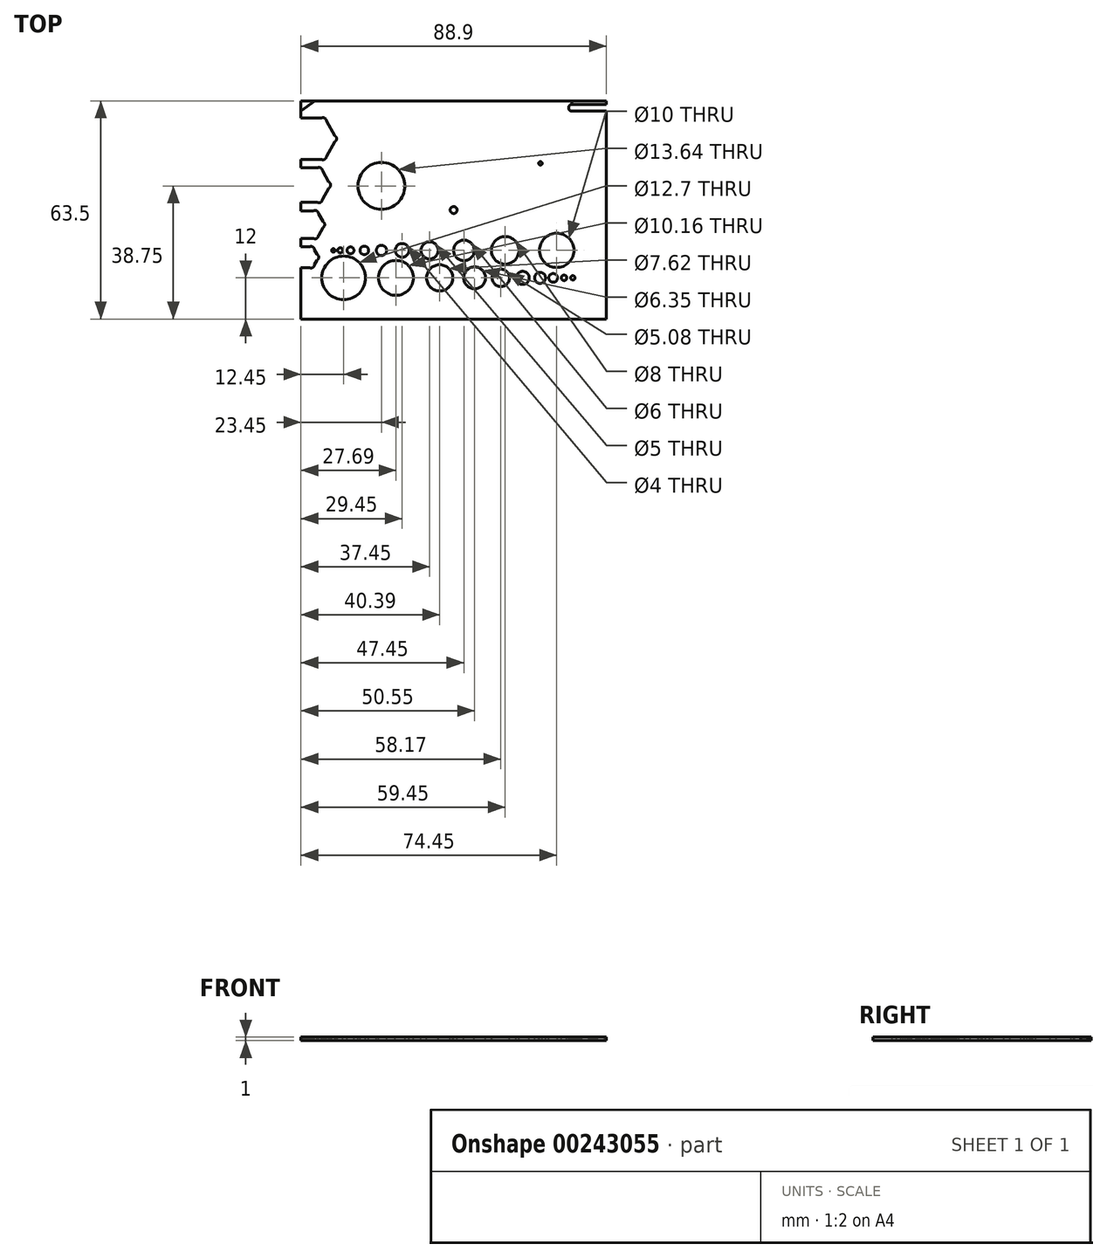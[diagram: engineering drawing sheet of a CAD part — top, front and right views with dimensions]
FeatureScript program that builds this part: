
annotation { "Feature Type Name" : "Feature", "Feature Type Description" : "" }
export const myFeature = defineFeature(function(context is Context, id is Id, definition is map)
    precondition{}
    {
        {
            var Q0;
            Q0=qCreatedBy(makeId("Top.planeOp"),FACE);
            var sketch = newSketch(context, id + "F0", { "sketchPlane" : qUnion([Q0])});
            skLineSegment(sketch, "E0.bottom", {"start": v(0, 0) * mm, "end": v(88.9, 0) * mm});
            skLineSegment(sketch, "E0.top", {"start": v(0, 63.5) * mm, "end": v(88.9, 63.5) * mm});
            skLineSegment(sketch, "E0.left", {"start": v(0, 0) * mm, "end": v(0, 63.5) * mm});
            skLineSegment(sketch, "E0.right", {"start": v(88.9, 0) * mm, "end": v(88.9, 63.5) * mm});
            skSolve(sketch);
        }
        {
            var Q0;
            Q0 = qSketchRegion(id + "F0", true);
            extrude(context, id + "F1", {"entities" : qUnion([Q0]), "depth" : 1 * mm});
        }
        {
            var Q0;
            Q0=makeQuery(id+"F1.opExtrude","CAP_FACE",FACE,{"disambiguationData":[OSD([sQuery(id+"F0.wireOp",EDGE,"E0.bottom"),sQuery(id+"F0.wireOp",EDGE,"E0.top"),sQuery(id+"F0.wireOp",EDGE,"E0.left"),sQuery(id+"F0.wireOp",EDGE,"E0.right")])],"isStart":false});
            var sketch = newSketch(context, id + "F2", { "sketchPlane" : qUnion([Q0])});
            skLineSegment(sketch, "E1", {"start": v(5.4, 0) * mm, "end": v(5.4, 2) * mm});
            skLineSegment(sketch, "E2", {"start": v(6.4, 0) * mm, "end": v(6.4, 1) * mm});
            skLineSegment(sketch, "E3", {"start": v(7.4, 0) * mm, "end": v(7.4, 1) * mm});
            skLineSegment(sketch, "E4", {"start": v(8.4, 0) * mm, "end": v(8.4, 1) * mm});
            skLineSegment(sketch, "E5", {"start": v(9.4, 0) * mm, "end": v(9.4, 1) * mm});
            skLineSegment(sketch, "E6", {"start": v(10.4, 0) * mm, "end": v(10.4, 1.5) * mm});
            skLineSegment(sketch, "E7", {"start": v(11.4, 0) * mm, "end": v(11.4, 1) * mm});
            skLineSegment(sketch, "E8", {"start": v(12.4, 0) * mm, "end": v(12.4, 1) * mm});
            skLineSegment(sketch, "E9", {"start": v(13.4, 0) * mm, "end": v(13.4, 1) * mm});
            skLineSegment(sketch, "E10", {"start": v(14.4, 0) * mm, "end": v(14.4, 1) * mm});
            skLineSegment(sketch, "E11", {"start": v(15.4, 0) * mm, "end": v(15.4, 2) * mm});
            skLineSegment(sketch, "E12.1.0.0", {"start": v(25.4, 0) * mm, "end": v(25.4, 2) * mm});
            skLineSegment(sketch, "E12.1.0.1", {"start": v(20.4, 0) * mm, "end": v(20.4, 1.5) * mm});
            skLineSegment(sketch, "E12.1.0.2", {"start": v(25.4, 0) * mm, "end": v(25.4, 2) * mm});
            skLineSegment(sketch, "E12.1.0.3", {"start": v(24.4, 0) * mm, "end": v(24.4, 1) * mm});
            skLineSegment(sketch, "E12.1.0.4", {"start": v(23.4, 0) * mm, "end": v(23.4, 1) * mm});
            skLineSegment(sketch, "E12.1.0.5", {"start": v(22.4, 0) * mm, "end": v(22.4, 1) * mm});
            skLineSegment(sketch, "E12.1.0.6", {"start": v(21.4, 0) * mm, "end": v(21.4, 1) * mm});
            skLineSegment(sketch, "E12.1.0.7", {"start": v(19.4, 0) * mm, "end": v(19.4, 1) * mm});
            skLineSegment(sketch, "E12.1.0.8", {"start": v(18.4, 0) * mm, "end": v(18.4, 1) * mm});
            skLineSegment(sketch, "E12.1.0.9", {"start": v(17.4, 0) * mm, "end": v(17.4, 1) * mm});
            skLineSegment(sketch, "E12.1.0.10", {"start": v(16.4, 0) * mm, "end": v(16.4, 1) * mm});
            skLineSegment(sketch, "E12.2.0.0", {"start": v(35.4, 0) * mm, "end": v(35.4, 2) * mm});
            skLineSegment(sketch, "E12.2.0.1", {"start": v(30.4, 0) * mm, "end": v(30.4, 1.5) * mm});
            skLineSegment(sketch, "E12.2.0.2", {"start": v(35.4, 0) * mm, "end": v(35.4, 2) * mm});
            skLineSegment(sketch, "E12.2.0.3", {"start": v(34.4, 0) * mm, "end": v(34.4, 1) * mm});
            skLineSegment(sketch, "E12.2.0.4", {"start": v(33.4, 0) * mm, "end": v(33.4, 1) * mm});
            skLineSegment(sketch, "E12.2.0.5", {"start": v(32.4, 0) * mm, "end": v(32.4, 1) * mm});
            skLineSegment(sketch, "E12.2.0.6", {"start": v(31.4, 0) * mm, "end": v(31.4, 1) * mm});
            skLineSegment(sketch, "E12.2.0.7", {"start": v(29.4, 0) * mm, "end": v(29.4, 1) * mm});
            skLineSegment(sketch, "E12.2.0.8", {"start": v(28.4, 0) * mm, "end": v(28.4, 1) * mm});
            skLineSegment(sketch, "E12.2.0.9", {"start": v(27.4, 0) * mm, "end": v(27.4, 1) * mm});
            skLineSegment(sketch, "E12.2.0.10", {"start": v(26.4, 0) * mm, "end": v(26.4, 1) * mm});
            skLineSegment(sketch, "E12.3.0.0", {"start": v(45.4, 0) * mm, "end": v(45.4, 2) * mm});
            skLineSegment(sketch, "E12.3.0.1", {"start": v(40.4, 0) * mm, "end": v(40.4, 1.5) * mm});
            skLineSegment(sketch, "E12.3.0.2", {"start": v(45.4, 0) * mm, "end": v(45.4, 2) * mm});
            skLineSegment(sketch, "E12.3.0.3", {"start": v(44.4, 0) * mm, "end": v(44.4, 1) * mm});
            skLineSegment(sketch, "E12.3.0.4", {"start": v(43.4, 0) * mm, "end": v(43.4, 1) * mm});
            skLineSegment(sketch, "E12.3.0.5", {"start": v(42.4, 0) * mm, "end": v(42.4, 1) * mm});
            skLineSegment(sketch, "E12.3.0.6", {"start": v(41.4, 0) * mm, "end": v(41.4, 1) * mm});
            skLineSegment(sketch, "E12.3.0.7", {"start": v(39.4, 0) * mm, "end": v(39.4, 1) * mm});
            skLineSegment(sketch, "E12.3.0.8", {"start": v(38.4, 0) * mm, "end": v(38.4, 1) * mm});
            skLineSegment(sketch, "E12.3.0.9", {"start": v(37.4, 0) * mm, "end": v(37.4, 1) * mm});
            skLineSegment(sketch, "E12.3.0.10", {"start": v(36.4, 0) * mm, "end": v(36.4, 1) * mm});
            skLineSegment(sketch, "E12.4.0.0", {"start": v(55.4, 0) * mm, "end": v(55.4, 2) * mm});
            skLineSegment(sketch, "E12.4.0.1", {"start": v(50.4, 0) * mm, "end": v(50.4, 1.5) * mm});
            skLineSegment(sketch, "E12.4.0.2", {"start": v(55.4, 0) * mm, "end": v(55.4, 2) * mm});
            skLineSegment(sketch, "E12.4.0.3", {"start": v(54.4, 0) * mm, "end": v(54.4, 1) * mm});
            skLineSegment(sketch, "E12.4.0.4", {"start": v(53.4, 0) * mm, "end": v(53.4, 1) * mm});
            skLineSegment(sketch, "E12.4.0.5", {"start": v(52.4, 0) * mm, "end": v(52.4, 1) * mm});
            skLineSegment(sketch, "E12.4.0.6", {"start": v(51.4, 0) * mm, "end": v(51.4, 1) * mm});
            skLineSegment(sketch, "E12.4.0.7", {"start": v(49.4, 0) * mm, "end": v(49.4, 1) * mm});
            skLineSegment(sketch, "E12.4.0.8", {"start": v(48.4, 0) * mm, "end": v(48.4, 1) * mm});
            skLineSegment(sketch, "E12.4.0.9", {"start": v(47.4, 0) * mm, "end": v(47.4, 1) * mm});
            skLineSegment(sketch, "E12.4.0.10", {"start": v(46.4, 0) * mm, "end": v(46.4, 1) * mm});
            skLineSegment(sketch, "E12.5.0.0", {"start": v(65.4, 0) * mm, "end": v(65.4, 2) * mm});
            skLineSegment(sketch, "E12.5.0.1", {"start": v(60.4, 0) * mm, "end": v(60.4, 1.5) * mm});
            skLineSegment(sketch, "E12.5.0.2", {"start": v(65.4, 0) * mm, "end": v(65.4, 2) * mm});
            skLineSegment(sketch, "E12.5.0.3", {"start": v(64.4, 0) * mm, "end": v(64.4, 1) * mm});
            skLineSegment(sketch, "E12.5.0.4", {"start": v(63.4, 0) * mm, "end": v(63.4, 1) * mm});
            skLineSegment(sketch, "E12.5.0.5", {"start": v(62.4, 0) * mm, "end": v(62.4, 1) * mm});
            skLineSegment(sketch, "E12.5.0.6", {"start": v(61.4, 0) * mm, "end": v(61.4, 1) * mm});
            skLineSegment(sketch, "E12.5.0.7", {"start": v(59.4, 0) * mm, "end": v(59.4, 1) * mm});
            skLineSegment(sketch, "E12.5.0.8", {"start": v(58.4, 0) * mm, "end": v(58.4, 1) * mm});
            skLineSegment(sketch, "E12.5.0.9", {"start": v(57.4, 0) * mm, "end": v(57.4, 1) * mm});
            skLineSegment(sketch, "E12.5.0.10", {"start": v(56.4, 0) * mm, "end": v(56.4, 1) * mm});
            skLineSegment(sketch, "E12.6.0.0", {"start": v(75.4, 0) * mm, "end": v(75.4, 2) * mm});
            skLineSegment(sketch, "E12.6.0.1", {"start": v(70.4, 0) * mm, "end": v(70.4, 1.5) * mm});
            skLineSegment(sketch, "E12.6.0.2", {"start": v(75.4, 0) * mm, "end": v(75.4, 2) * mm});
            skLineSegment(sketch, "E12.6.0.3", {"start": v(74.4, 0) * mm, "end": v(74.4, 1) * mm});
            skLineSegment(sketch, "E12.6.0.4", {"start": v(73.4, 0) * mm, "end": v(73.4, 1) * mm});
            skLineSegment(sketch, "E12.6.0.5", {"start": v(72.4, 0) * mm, "end": v(72.4, 1) * mm});
            skLineSegment(sketch, "E12.6.0.6", {"start": v(71.4, 0) * mm, "end": v(71.4, 1) * mm});
            skLineSegment(sketch, "E12.6.0.7", {"start": v(69.4, 0) * mm, "end": v(69.4, 1) * mm});
            skLineSegment(sketch, "E12.6.0.8", {"start": v(68.4, 0) * mm, "end": v(68.4, 1) * mm});
            skLineSegment(sketch, "E12.6.0.9", {"start": v(67.4, 0) * mm, "end": v(67.4, 1) * mm});
            skLineSegment(sketch, "E12.6.0.10", {"start": v(66.4, 0) * mm, "end": v(66.4, 1) * mm});
            skLineSegment(sketch, "E12.7.0.0", {"start": v(85.4, 0) * mm, "end": v(85.4, 2) * mm});
            skLineSegment(sketch, "E12.7.0.1", {"start": v(80.4, 0) * mm, "end": v(80.4, 1.5) * mm});
            skLineSegment(sketch, "E12.7.0.2", {"start": v(85.4, 0) * mm, "end": v(85.4, 2) * mm});
            skLineSegment(sketch, "E12.7.0.3", {"start": v(84.4, 0) * mm, "end": v(84.4, 1) * mm});
            skLineSegment(sketch, "E12.7.0.4", {"start": v(83.4, 0) * mm, "end": v(83.4, 1) * mm});
            skLineSegment(sketch, "E12.7.0.5", {"start": v(82.4, 0) * mm, "end": v(82.4, 1) * mm});
            skLineSegment(sketch, "E12.7.0.6", {"start": v(81.4, 0) * mm, "end": v(81.4, 1) * mm});
            skLineSegment(sketch, "E12.7.0.7", {"start": v(79.4, 0) * mm, "end": v(79.4, 1) * mm});
            skLineSegment(sketch, "E12.7.0.8", {"start": v(78.4, 0) * mm, "end": v(78.4, 1) * mm});
            skLineSegment(sketch, "E12.7.0.9", {"start": v(77.4, 0) * mm, "end": v(77.4, 1) * mm});
            skLineSegment(sketch, "E12.7.0.10", {"start": v(76.4, 0) * mm, "end": v(76.4, 1) * mm});
            skLineSegment(sketch, "E12.direction1", {"start": v(6.4, 0) * mm, "end": v(16.4, 0) * mm, "construction": true});
            skLineSegment(sketch, "E13", {"start": v(0, 2.5) * mm, "end": v(88.9, 2.5) * mm, "construction": true});
            skText(sketch, "E14", { "text": "1", "fontName": "NotoSansCJKjp-Regular.otf"});
            skText(sketch, "E15", { "text": "0", "fontName": "NotoSansCJKjp-Regular.otf"});
            skText(sketch, "E16", { "text": "2", "fontName": "NotoSansCJKjp-Regular.otf"});
            skText(sketch, "E17", { "text": "3", "fontName": "NotoSansCJKjp-Regular.otf"});
            skText(sketch, "E18", { "text": "4", "fontName": "NotoSansCJKjp-Regular.otf"});
            skText(sketch, "E19", { "text": "5", "fontName": "NotoSansCJKjp-Regular.otf"});
            skText(sketch, "E20", { "text": "6", "fontName": "NotoSansCJKjp-Regular.otf"});
            skText(sketch, "E21", { "text": "7", "fontName": "NotoSansCJKjp-Regular.otf"});
            skText(sketch, "E22", { "text": "8", "fontName": "NotoSansCJKjp-Regular.otf"});
            const initialGuessF2  = {"E14": [0.0148, 0.0025, 1, 0, 0.0016], "E15": [0.00478, 0.0025, 1, 0, 0.00158], "E16": [0.02479, 0.0025, 1, 0, 0.00158], "E17": [0.03479, 0.0025, 1, 0, 0.00158], "E18": [0.04477, 0.0025, 1, 0, 0.00156], "E19": [0.05479, 0.0025, 1, 0, 0.00158], "E20": [0.06478, 0.0025, 1, 0, 0.00157], "E21": [0.07478, 0.0025, 1, 0, 0.00157], "E22": [0.08478, 0.0025, 1, 0, 0.00157]};
            skSetInitialGuess(sketch, initialGuessF2);
            skSolve(sketch);
        }
        {
            var Q0;
            Q0=makeQuery(id+"F1.opExtrude","CAP_FACE",FACE,{"disambiguationData":[OSD([sQuery(id+"F0.wireOp",EDGE,"E0.bottom"),sQuery(id+"F0.wireOp",EDGE,"E0.top"),sQuery(id+"F0.wireOp",EDGE,"E0.left"),sQuery(id+"F0.wireOp",EDGE,"E0.right")])],"isStart":true});
            var sketch = newSketch(context, id + "F3", { "sketchPlane" : qUnion([Q0])});
            skPoint(sketch, "E23.0", {"position": v(5.4, -2) * mm});
            skPoint(sketch, "E24.0", {"position": v(10.4, -1.5) * mm});
            skLineSegment(sketch, "E25.0", {"start": v(0, -2.5) * mm, "end": v(88.9, -2.5) * mm});
            skPoint(sketch, "E26.0", {"position": v(6.4, -1) * mm});
            skLineSegment(sketch, "E27", {"start": v(5.4, -2) * mm, "end": v(5.4, 0) * mm});
            skLineSegment(sketch, "E28", {"start": v(10.48, 0) * mm, "end": v(10.48, -1) * mm});
            skLineSegment(sketch, "E29", {"start": v(7.94, 0) * mm, "end": v(7.94, -1) * mm});
            skLineSegment(sketch, "E30", {"start": v(13.02, 0) * mm, "end": v(13.02, -1) * mm});
            skLineSegment(sketch, "E31", {"start": v(15.56, 0) * mm, "end": v(15.56, -1) * mm});
            skLineSegment(sketch, "E32", {"start": v(18.1, 0) * mm, "end": v(18.1, -1.5) * mm});
            skLineSegment(sketch, "E33", {"start": v(20.64, 0) * mm, "end": v(20.64, -1) * mm});
            skLineSegment(sketch, "E34", {"start": v(23.18, 0) * mm, "end": v(23.18, -1) * mm});
            skLineSegment(sketch, "E35", {"start": v(25.72, 0) * mm, "end": v(25.72, -1) * mm});
            skLineSegment(sketch, "E36", {"start": v(28.26, 0) * mm, "end": v(28.26, -1) * mm});
            skLineSegment(sketch, "E37", {"start": v(30.8, 0) * mm, "end": v(30.8, -2) * mm});
            skPoint(sketch, "E38.1.0.0", {"position": v(31.8, -1) * mm});
            skPoint(sketch, "E38.1.0.1", {"position": v(35.8, -1.5) * mm});
            skLineSegment(sketch, "E38.1.0.2", {"start": v(56.2, 0) * mm, "end": v(56.2, -2) * mm});
            skLineSegment(sketch, "E38.1.0.3", {"start": v(38.42, 0) * mm, "end": v(38.42, -1) * mm});
            skLineSegment(sketch, "E38.1.0.4", {"start": v(51.12, 0) * mm, "end": v(51.12, -1) * mm});
            skLineSegment(sketch, "E38.1.0.5", {"start": v(40.96, 0) * mm, "end": v(40.96, -1) * mm});
            skLineSegment(sketch, "E38.1.0.6", {"start": v(43.5, 0) * mm, "end": v(43.5, -1.5) * mm});
            skLineSegment(sketch, "E38.1.0.7", {"start": v(46.04, 0) * mm, "end": v(46.04, -1) * mm});
            skLineSegment(sketch, "E38.1.0.8", {"start": v(33.34, 0) * mm, "end": v(33.34, -1) * mm});
            skLineSegment(sketch, "E38.1.0.9", {"start": v(35.88, 0) * mm, "end": v(35.88, -1) * mm});
            skLineSegment(sketch, "E38.1.0.10", {"start": v(48.58, 0) * mm, "end": v(48.58, -1) * mm});
            skLineSegment(sketch, "E38.1.0.11", {"start": v(53.66, 0) * mm, "end": v(53.66, -1) * mm});
            skPoint(sketch, "E38.2.0.0", {"position": v(57.2, -1) * mm});
            skPoint(sketch, "E38.2.0.1", {"position": v(61.2, -1.5) * mm});
            skLineSegment(sketch, "E38.2.0.2", {"start": v(81.6, 0) * mm, "end": v(81.6, -2) * mm});
            skLineSegment(sketch, "E38.2.0.3", {"start": v(63.82, 0) * mm, "end": v(63.82, -1) * mm});
            skLineSegment(sketch, "E38.2.0.4", {"start": v(76.52, 0) * mm, "end": v(76.52, -1) * mm});
            skLineSegment(sketch, "E38.2.0.5", {"start": v(66.36, 0) * mm, "end": v(66.36, -1) * mm});
            skLineSegment(sketch, "E38.2.0.6", {"start": v(68.9, 0) * mm, "end": v(68.9, -1.5) * mm});
            skLineSegment(sketch, "E38.2.0.7", {"start": v(71.44, 0) * mm, "end": v(71.44, -1) * mm});
            skLineSegment(sketch, "E38.2.0.8", {"start": v(58.74, 0) * mm, "end": v(58.74, -1) * mm});
            skLineSegment(sketch, "E38.2.0.9", {"start": v(61.28, 0) * mm, "end": v(61.28, -1) * mm});
            skLineSegment(sketch, "E38.2.0.10", {"start": v(73.98, 0) * mm, "end": v(73.98, -1) * mm});
            skLineSegment(sketch, "E38.2.0.11", {"start": v(79.06, 0) * mm, "end": v(79.06, -1) * mm});
            skLineSegment(sketch, "E38.direction1", {"start": v(6.4, -1) * mm, "end": v(31.8, -1) * mm, "construction": true});
            skText(sketch, "E39", { "text": "0", "fontName": "NotoSansCJKjp-Regular.otf"});
            skText(sketch, "E40", { "text": "1", "fontName": "NotoSansCJKjp-Regular.otf"});
            skText(sketch, "E41", { "text": "2", "fontName": "NotoSansCJKjp-Regular.otf"});
            skText(sketch, "E42", { "text": "3", "fontName": "NotoSansCJKjp-Regular.otf"});
            const initialGuessF3  = {"E39": [0.00478, -0.00408, 1, 0, 0.00158], "E40": [0.0302, -0.0041, 1, 0, 0.0016], "E41": [0.05559, -0.00408, 1, 0, 0.00158], "E42": [0.08099, -0.00408, 1, 0, 0.00158]};
            skSetInitialGuess(sketch, initialGuessF3);
            skSolve(sketch);
        }
        {
            var Q0;
            Q0=makeQuery(id+"F2.imprint","IMPRINT",FACE,{"disambiguationData":[TD([[makeQuery(id+"F2.imprint","IMPRINT",EDGE,{"derivedFrom":sQuery(id+"F2.wireOp",EDGE,"E14.sketch_text.stroke-0")}),-1.0]])]});
            var sketch = newSketch(context, id + "F4", { "sketchPlane" : qUnion([Q0])});
            skLineSegment(sketch, "E43.0", {"start": v(88.9, 0) * mm, "end": v(88.9, 63.5) * mm});
            skLineSegment(sketch, "E44.0", {"start": v(0, 0) * mm, "end": v(88.9, 0) * mm});
            skLineSegment(sketch, "E45", {"start": v(88.9, 31.75) * mm, "end": v(0, 31.75) * mm, "construction": true});
            skLineSegment(sketch, "E46", {"start": v(88.9, 62.5) * mm, "end": v(78.9, 62.5) * mm});
            skLineSegment(sketch, "E47", {"start": v(78.9, 62.5) * mm, "end": v(78.9, 60.5) * mm});
            skLineSegment(sketch, "E48", {"start": v(78.9, 60.5) * mm, "end": v(88.9, 60.5) * mm});
            skCircle(sketch, "E49", {"center": v(78.9, 61.5) * mm, "radius": 1 * mm});
            skSolve(sketch);
        }
        {
            var Q0;
            Q0 = qSketchRegion(id + "F4", true);
            extrude(context, id + "F5", {"entities" : qUnion([Q0]), "operationType" : NewBodyOperationType.REMOVE, "oppositeDirection" : true, "depth" : 25 * mm});
        }
        {
            var Q0;
            {var subQ0=sQuery(id+"F0.wireOp",EDGE,"E0.bottom");var subQ1=sQuery(id+"F0.wireOp",EDGE,"E0.right");Q0=makeQuery(id+"F5.boolean.opBoolean","SPLIT",FACE,{"disambiguationData":[TD([makeQuery(id+"F1.opExtrude","SWEPT_FACE",FACE,{"disambiguationData":[OSD([subQ0])]})])],"derivedFrom":makeQuery(id+"F1.opExtrude","SWEPT_FACE",FACE,{"disambiguationData":[OSD([subQ1])]})});}
            var sketch = newSketch(context, id + "F6", { "sketchPlane" : qUnion([Q0])});
            skLineSegment(sketch, "E50.0.0", {"start": v(62.5, 1) * mm, "end": v(62.5, 0) * mm});
            skLineSegment(sketch, "E50.0.1", {"start": v(62.5, 0) * mm, "end": v(63.5, 0) * mm});
            skLineSegment(sketch, "E50.0.2", {"start": v(63.5, 0) * mm, "end": v(63.5, 1) * mm});
            skLineSegment(sketch, "E50.0.3", {"start": v(63.5, 1) * mm, "end": v(62.5, 1) * mm});
            skPoint(sketch, "E51.endSnap0", {"position": v(63.5, 0.5) * mm});
            skPoint(sketch, "E52.endSnap0", {"position": v(63, 1) * mm});
            skLineSegment(sketch, "E53.0.0", {"start": v(62.5, 0) * mm, "end": v(62.5, 1) * mm});
            skPoint(sketch, "E54", {"position": v(62.5, 0.5) * mm});
            skEllipse(sketch, "E55", {"center": v(62.5, 1) * mm, "majorRadius": 1 * mm, "minorRadius": 0.5 * mm, "majorAxis": v(1, 0)});
            skEllipse(sketch, "E56", {"center": v(62.5, 0) * mm, "majorRadius": 1 * mm, "minorRadius": 0.5 * mm, "majorAxis": v(1, 0)});
            skSolve(sketch);
        }
        {
            var Q0;
            {var subQ0=sQuery(id+"F6.wireOp",EDGE,"E50.0.1");Q0=makeQuery(id+"F6.imprint","IMPRINT",FACE,{"disambiguationData":[TD([[makeQuery(id+"F6.imprint","IMPRINT",EDGE,{"derivedFrom":subQ0}),1.0]])]});}
            var Q1;
            {var subQ0=sQuery(id+"F6.wireOp",EDGE,"E50.0.3");Q1=makeQuery(id+"F6.imprint","IMPRINT",FACE,{"disambiguationData":[TD([[makeQuery(id+"F6.imprint","IMPRINT",EDGE,{"derivedFrom":subQ0}),1.0]])]});}
            extrude(context, id + "F7", {"entities" : qUnion([Q0, Q1]), "operationType" : NewBodyOperationType.REMOVE, "oppositeDirection" : true, "depth" : 10 * mm});
        }
        {
            var Q0;
            Q0=makeQuery(id+"F2.imprint","IMPRINT",FACE,{"disambiguationData":[TD([[makeQuery(id+"F2.imprint","IMPRINT",EDGE,{"derivedFrom":sQuery(id+"F2.wireOp",EDGE,"E14.sketch_text.stroke-0")}),-1.0]])]});
            var sketch = newSketch(context, id + "F8", { "sketchPlane" : qUnion([Q0])});
            skLineSegment(sketch, "E57.0.0", {"start": v(88.9, 63.5) * mm, "end": v(0, 63.5) * mm});
            skLineSegment(sketch, "E57.0.1", {"start": v(-4.62, 60.5) * mm, "end": v(50.37, 28.75) * mm, "construction": true});
            skLineSegment(sketch, "E57.0.2", {"start": v(0, 0) * mm, "end": v(5.4, 0) * mm});
            skLineSegment(sketch, "E57.0.3", {"start": v(5.4, 0) * mm, "end": v(6.4, 0) * mm});
            skLineSegment(sketch, "E57.0.4", {"start": v(6.4, 0) * mm, "end": v(7.4, 0) * mm});
            skLineSegment(sketch, "E57.0.5", {"start": v(7.4, 0) * mm, "end": v(8.4, 0) * mm});
            skLineSegment(sketch, "E57.0.6", {"start": v(8.4, 0) * mm, "end": v(9.4, 0) * mm});
            skLineSegment(sketch, "E57.0.7", {"start": v(9.4, 0) * mm, "end": v(10.4, 0) * mm});
            skLineSegment(sketch, "E57.0.8", {"start": v(10.4, 0) * mm, "end": v(11.4, 0) * mm});
            skLineSegment(sketch, "E57.0.9", {"start": v(11.4, 0) * mm, "end": v(12.4, 0) * mm});
            skLineSegment(sketch, "E57.0.10", {"start": v(12.4, 0) * mm, "end": v(13.4, 0) * mm});
            skLineSegment(sketch, "E57.0.11", {"start": v(13.4, 0) * mm, "end": v(14.4, 0) * mm});
            skLineSegment(sketch, "E57.0.12", {"start": v(14.4, 0) * mm, "end": v(15.4, 0) * mm});
            skLineSegment(sketch, "E57.0.13", {"start": v(15.4, 0) * mm, "end": v(16.4, 0) * mm});
            skLineSegment(sketch, "E57.0.14", {"start": v(16.4, 0) * mm, "end": v(17.4, 0) * mm});
            skLineSegment(sketch, "E57.0.15", {"start": v(17.4, 0) * mm, "end": v(18.4, 0) * mm});
            skLineSegment(sketch, "E57.0.16", {"start": v(18.4, 0) * mm, "end": v(19.4, 0) * mm});
            skLineSegment(sketch, "E57.0.17", {"start": v(19.4, 0) * mm, "end": v(20.4, 0) * mm});
            skLineSegment(sketch, "E57.0.18", {"start": v(20.4, 0) * mm, "end": v(21.4, 0) * mm});
            skLineSegment(sketch, "E57.0.19", {"start": v(21.4, 0) * mm, "end": v(22.4, 0) * mm});
            skLineSegment(sketch, "E57.0.20", {"start": v(22.4, 0) * mm, "end": v(23.4, 0) * mm});
            skLineSegment(sketch, "E57.0.21", {"start": v(23.4, 0) * mm, "end": v(24.4, 0) * mm});
            skLineSegment(sketch, "E57.0.22", {"start": v(24.4, 0) * mm, "end": v(25.4, 0) * mm});
            skLineSegment(sketch, "E57.0.23", {"start": v(25.4, 0) * mm, "end": v(26.4, 0) * mm});
            skLineSegment(sketch, "E57.0.24", {"start": v(26.4, 0) * mm, "end": v(27.4, 0) * mm});
            skLineSegment(sketch, "E57.0.25", {"start": v(27.4, 0) * mm, "end": v(28.4, 0) * mm});
            skLineSegment(sketch, "E57.0.26", {"start": v(28.4, 0) * mm, "end": v(29.4, 0) * mm});
            skLineSegment(sketch, "E57.0.27", {"start": v(29.4, 0) * mm, "end": v(30.4, 0) * mm});
            skLineSegment(sketch, "E57.0.28", {"start": v(30.4, 0) * mm, "end": v(31.4, 0) * mm});
            skLineSegment(sketch, "E57.0.29", {"start": v(31.4, 0) * mm, "end": v(32.4, 0) * mm});
            skLineSegment(sketch, "E57.0.30", {"start": v(32.4, 0) * mm, "end": v(33.4, 0) * mm});
            skLineSegment(sketch, "E57.0.31", {"start": v(33.4, 0) * mm, "end": v(34.4, 0) * mm});
            skLineSegment(sketch, "E57.0.32", {"start": v(34.4, 0) * mm, "end": v(35.4, 0) * mm});
            skLineSegment(sketch, "E57.0.33", {"start": v(35.4, 0) * mm, "end": v(36.4, 0) * mm});
            skLineSegment(sketch, "E57.0.34", {"start": v(36.4, 0) * mm, "end": v(37.4, 0) * mm});
            skLineSegment(sketch, "E57.0.35", {"start": v(37.4, 0) * mm, "end": v(38.4, 0) * mm});
            skLineSegment(sketch, "E57.0.36", {"start": v(38.4, 0) * mm, "end": v(39.4, 0) * mm});
            skLineSegment(sketch, "E57.0.37", {"start": v(39.4, 0) * mm, "end": v(40.4, 0) * mm});
            skLineSegment(sketch, "E57.0.38", {"start": v(40.4, 0) * mm, "end": v(41.4, 0) * mm});
            skLineSegment(sketch, "E57.0.39", {"start": v(41.4, 0) * mm, "end": v(42.4, 0) * mm});
            skLineSegment(sketch, "E57.0.40", {"start": v(42.4, 0) * mm, "end": v(43.4, 0) * mm});
            skLineSegment(sketch, "E57.0.41", {"start": v(43.4, 0) * mm, "end": v(44.4, 0) * mm});
            skLineSegment(sketch, "E57.0.42", {"start": v(44.4, 0) * mm, "end": v(45.4, 0) * mm});
            skLineSegment(sketch, "E57.0.43", {"start": v(45.4, 0) * mm, "end": v(46.4, 0) * mm});
            skLineSegment(sketch, "E57.0.44", {"start": v(46.4, 0) * mm, "end": v(47.4, 0) * mm});
            skLineSegment(sketch, "E57.0.45", {"start": v(47.4, 0) * mm, "end": v(48.4, 0) * mm});
            skLineSegment(sketch, "E57.0.46", {"start": v(48.4, 0) * mm, "end": v(49.4, 0) * mm});
            skLineSegment(sketch, "E57.0.47", {"start": v(49.4, 0) * mm, "end": v(50.4, 0) * mm});
            skLineSegment(sketch, "E57.0.48", {"start": v(50.4, 0) * mm, "end": v(51.4, 0) * mm});
            skLineSegment(sketch, "E57.0.49", {"start": v(51.4, 0) * mm, "end": v(52.4, 0) * mm});
            skLineSegment(sketch, "E57.0.50", {"start": v(52.4, 0) * mm, "end": v(53.4, 0) * mm});
            skLineSegment(sketch, "E57.0.51", {"start": v(53.4, 0) * mm, "end": v(54.4, 0) * mm});
            skLineSegment(sketch, "E57.0.52", {"start": v(54.4, 0) * mm, "end": v(55.4, 0) * mm});
            skLineSegment(sketch, "E57.0.53", {"start": v(55.4, 0) * mm, "end": v(56.4, 0) * mm});
            skLineSegment(sketch, "E57.0.54", {"start": v(56.4, 0) * mm, "end": v(57.4, 0) * mm});
            skLineSegment(sketch, "E57.0.55", {"start": v(57.4, 0) * mm, "end": v(58.4, 0) * mm});
            skLineSegment(sketch, "E57.0.56", {"start": v(58.4, 0) * mm, "end": v(59.4, 0) * mm});
            skLineSegment(sketch, "E57.0.57", {"start": v(59.4, 0) * mm, "end": v(60.4, 0) * mm});
            skLineSegment(sketch, "E57.0.58", {"start": v(60.4, 0) * mm, "end": v(61.4, 0) * mm});
            skLineSegment(sketch, "E57.0.59", {"start": v(61.4, 0) * mm, "end": v(62.4, 0) * mm});
            skLineSegment(sketch, "E57.0.60", {"start": v(62.4, 0) * mm, "end": v(63.4, 0) * mm});
            skLineSegment(sketch, "E57.0.61", {"start": v(63.4, 0) * mm, "end": v(64.4, 0) * mm});
            skLineSegment(sketch, "E57.0.62", {"start": v(64.4, 0) * mm, "end": v(65.4, 0) * mm});
            skLineSegment(sketch, "E57.0.63", {"start": v(65.4, 0) * mm, "end": v(66.4, 0) * mm});
            skLineSegment(sketch, "E57.0.64", {"start": v(66.4, 0) * mm, "end": v(67.4, 0) * mm});
            skLineSegment(sketch, "E57.0.65", {"start": v(67.4, 0) * mm, "end": v(68.4, 0) * mm});
            skLineSegment(sketch, "E57.0.66", {"start": v(68.4, 0) * mm, "end": v(69.4, 0) * mm});
            skLineSegment(sketch, "E57.0.67", {"start": v(69.4, 0) * mm, "end": v(70.4, 0) * mm});
            skLineSegment(sketch, "E57.0.68", {"start": v(70.4, 0) * mm, "end": v(71.4, 0) * mm});
            skLineSegment(sketch, "E57.0.69", {"start": v(71.4, 0) * mm, "end": v(72.4, 0) * mm});
            skLineSegment(sketch, "E57.0.70", {"start": v(72.4, 0) * mm, "end": v(73.4, 0) * mm});
            skLineSegment(sketch, "E57.0.71", {"start": v(73.4, 0) * mm, "end": v(74.4, 0) * mm});
            skLineSegment(sketch, "E57.0.72", {"start": v(74.4, 0) * mm, "end": v(75.4, 0) * mm});
            skLineSegment(sketch, "E57.0.73", {"start": v(75.4, 0) * mm, "end": v(76.4, 0) * mm});
            skLineSegment(sketch, "E57.0.74", {"start": v(76.4, 0) * mm, "end": v(77.4, 0) * mm});
            skLineSegment(sketch, "E57.0.75", {"start": v(77.4, 0) * mm, "end": v(78.4, 0) * mm});
            skLineSegment(sketch, "E57.0.76", {"start": v(78.4, 0) * mm, "end": v(79.4, 0) * mm});
            skLineSegment(sketch, "E57.0.77", {"start": v(79.4, 0) * mm, "end": v(80.4, 0) * mm});
            skLineSegment(sketch, "E57.0.78", {"start": v(80.4, 0) * mm, "end": v(81.4, 0) * mm});
            skLineSegment(sketch, "E57.0.79", {"start": v(81.4, 0) * mm, "end": v(82.4, 0) * mm});
            skLineSegment(sketch, "E57.0.80", {"start": v(82.4, 0) * mm, "end": v(83.4, 0) * mm});
            skLineSegment(sketch, "E57.0.81", {"start": v(83.4, 0) * mm, "end": v(84.4, 0) * mm});
            skLineSegment(sketch, "E57.0.82", {"start": v(84.4, 0) * mm, "end": v(85.4, 0) * mm});
            skLineSegment(sketch, "E57.0.83", {"start": v(85.4, 0) * mm, "end": v(88.9, 0) * mm});
            skLineSegment(sketch, "E57.0.84", {"start": v(88.9, 0) * mm, "end": v(88.9, 63.5) * mm});
            skCircle(sketch, "E58.cCircle", {"center": v(1.73, 18) * mm, "radius": 3 * mm, "construction": true});
            skLineSegment(sketch, "E58.0", {"start": v(2.46, 15) * mm, "end": v(0, 15) * mm});
            skLineSegment(sketch, "E58.1", {"start": v(0, 15) * mm, "end": v(-1.73, 18) * mm});
            skLineSegment(sketch, "E58.2", {"start": v(-1.73, 18) * mm, "end": v(0, 21) * mm});
            skLineSegment(sketch, "E58.3", {"start": v(0, 21) * mm, "end": v(2.46, 21) * mm});
            skLineSegment(sketch, "E58.4", {"start": v(3.96, 20.13) * mm, "end": v(4.7, 18.87) * mm});
            skLineSegment(sketch, "E58.5", {"start": v(4.7, 17.13) * mm, "end": v(3.96, 15.87) * mm});
            skPoint(sketch, "E58.0.midPoint", {"position": v(1.73, 15) * mm});
            skCircle(sketch, "E59.cCircle", {"center": v(2.3, 27.5) * mm, "radius": 4 * mm, "construction": true});
            skLineSegment(sketch, "E59.0", {"start": v(3.62, 23.5) * mm, "end": v(0, 23.5) * mm});
            skLineSegment(sketch, "E59.1", {"start": v(0, 23.5) * mm, "end": v(-2.3, 27.5) * mm});
            skLineSegment(sketch, "E59.2", {"start": v(-2.3, 27.5) * mm, "end": v(0, 31.5) * mm});
            skLineSegment(sketch, "E59.3", {"start": v(0, 31.5) * mm, "end": v(3.62, 31.5) * mm});
            skLineSegment(sketch, "E59.4", {"start": v(5.12, 30.63) * mm, "end": v(6.43, 28.37) * mm});
            skLineSegment(sketch, "E59.5", {"start": v(6.43, 26.63) * mm, "end": v(5.12, 24.37) * mm});
            skPoint(sketch, "E59.0.midPoint", {"position": v(2.3, 23.5) * mm});
            skCircle(sketch, "E60.cCircle", {"center": v(2.89, 39) * mm, "radius": 5 * mm, "construction": true});
            skLineSegment(sketch, "E60.0", {"start": v(5.77, 34) * mm, "end": v(5.2, 34) * mm});
            skLineSegment(sketch, "E60.1", {"start": v(0, 34) * mm, "end": v(-2.89, 39) * mm});
            skLineSegment(sketch, "E60.2", {"start": v(-2.89, 39) * mm, "end": v(0, 44) * mm});
            skLineSegment(sketch, "E60.3", {"start": v(0, 44) * mm, "end": v(4.77, 44) * mm});
            skLineSegment(sketch, "E60.4", {"start": v(6.27, 43.13) * mm, "end": v(8.16, 39.87) * mm});
            skLineSegment(sketch, "E60.5", {"start": v(8.16, 38.13) * mm, "end": v(6.27, 34.87) * mm});
            skPoint(sketch, "E60.0.midPoint", {"position": v(5.2, 34) * mm});
            skCircle(sketch, "E61.cCircle", {"center": v(3.46, 52.5) * mm, "radius": 6 * mm, "construction": true});
            skLineSegment(sketch, "E61.0", {"start": v(5.93, 46.5) * mm, "end": v(0, 46.5) * mm});
            skLineSegment(sketch, "E61.1", {"start": v(0, 46.5) * mm, "end": v(-3.46, 52.5) * mm});
            skLineSegment(sketch, "E61.2", {"start": v(-3.46, 52.5) * mm, "end": v(0, 58.5) * mm});
            skLineSegment(sketch, "E61.3", {"start": v(0, 58.5) * mm, "end": v(5.93, 58.5) * mm});
            skLineSegment(sketch, "E61.4", {"start": v(7.43, 57.63) * mm, "end": v(9.9, 53.37) * mm});
            skLineSegment(sketch, "E61.5", {"start": v(9.9, 51.63) * mm, "end": v(7.43, 47.37) * mm});
            skPoint(sketch, "E61.0.midPoint", {"position": v(3.46, 46.5) * mm});
            skLineSegment(sketch, "E62.bottom", {"start": v(0, 0) * mm, "end": v(12.45, 0) * mm, "construction": true});
            skLineSegment(sketch, "E62.top", {"start": v(1.73, 20) * mm, "end": v(11.18, 20) * mm, "construction": true});
            skLineSegment(sketch, "E62.left", {"start": v(1.73, 0) * mm, "end": v(1.73, 20) * mm, "construction": true});
            skLineSegment(sketch, "E62.right", {"start": v(12.45, 0) * mm, "end": v(12.45, 20) * mm, "construction": true});
            skCircle(sketch, "E63", {"center": v(9.45, 20) * mm, "radius": 0.5 * mm});
            skCircle(sketch, "E64", {"center": v(11.45, 20) * mm, "radius": 0.75 * mm});
            skCircle(sketch, "E65", {"center": v(14.45, 20) * mm, "radius": 1 * mm});
            skCircle(sketch, "E66", {"center": v(18.45, 20) * mm, "radius": 1.25 * mm});
            skCircle(sketch, "E67", {"center": v(23.45, 20) * mm, "radius": 1.5 * mm});
            skCircle(sketch, "E68", {"center": v(29.45, 20) * mm, "radius": 2 * mm});
            skCircle(sketch, "E69", {"center": v(37.45, 20) * mm, "radius": 2.5 * mm});
            skCircle(sketch, "E70", {"center": v(47.45, 20) * mm, "radius": 3 * mm});
            skCircle(sketch, "E71", {"center": v(59.45, 20) * mm, "radius": 4 * mm});
            skCircle(sketch, "E72", {"center": v(74.45, 20) * mm, "radius": 5 * mm});
            skCircle(sketch, "E73", {"center": v(12.45, 12) * mm, "radius": 6.35 * mm});
            skCircle(sketch, "E74", {"center": v(27.69, 12) * mm, "radius": 5.08 * mm});
            skCircle(sketch, "E75", {"center": v(40.4, 12) * mm, "radius": 3.81 * mm});
            skCircle(sketch, "E76", {"center": v(58.17, 12) * mm, "radius": 2.54 * mm});
            skCircle(sketch, "E77", {"center": v(64.52, 12) * mm, "radius": 1.9 * mm});
            skCircle(sketch, "E78", {"center": v(69.6, 12) * mm, "radius": 1.59 * mm});
            skCircle(sketch, "E79", {"center": v(73.4, 12) * mm, "radius": 1.27 * mm});
            skCircle(sketch, "E80", {"center": v(76.58, 12) * mm, "radius": 0.8 * mm});
            skCircle(sketch, "E81", {"center": v(50.55, 12) * mm, "radius": 3.18 * mm});
            skCircle(sketch, "E82", {"center": v(79.12, 12) * mm, "radius": 0.64 * mm});
            skArc(sketch, "E83", {"start": v(9.9, 51.63) * mm, "mid": v(10.4, 52.5) * mm, "end": v(9.9, 53.37) * mm});
            skArc(sketch, "E84", {"start": v(5.09, 24.62) * mm, "mid": v(3.62, 25.23) * mm, "end": v(3.41, 23.66) * mm});
            skArc(sketch, "E85", {"start": v(3.96, 20.13) * mm, "mid": v(3.46, 21) * mm, "end": v(2.46, 21) * mm});
            skArc(sketch, "E86", {"start": v(6.27, 43.13) * mm, "mid": v(5.77, 44) * mm, "end": v(4.77, 44) * mm});
            skArc(sketch, "E87", {"start": v(14.45, 39) * mm, "mid": v(27.89, 33.44) * mm, "end": v(33.45, 20) * mm, "construction": true});
            skArc(sketch, "E88.0.startCap", {"start": v(14.45, 38) * mm, "mid": v(13.45, 39) * mm, "end": v(14.45, 40) * mm, "construction": true});
            skArc(sketch, "E88.0.endCap", {"start": v(34.45, 20) * mm, "mid": v(33.45, 19) * mm, "end": v(32.45, 20) * mm, "construction": true});
            skArc(sketch, "E88.0.left", {"start": v(14.45, 40) * mm, "mid": v(28.6, 34.14) * mm, "end": v(34.45, 20) * mm, "construction": true});
            skArc(sketch, "E88.0.right", {"start": v(14.45, 38) * mm, "mid": v(27.18, 32.73) * mm, "end": v(32.45, 20) * mm, "construction": true});
            skCircle(sketch, "E89", {"center": v(69.72, 45.34) * mm, "radius": 11.88 * mm});
            skLineSegment(sketch, "E90", {"start": v(67.97, 33.58) * mm, "end": v(67.97, 42.21) * mm});
            skLineSegment(sketch, "E91", {"start": v(68.01, 41) * mm, "end": v(60.54, 36.69) * mm});
            skLineSegment(sketch, "E92", {"start": v(68.97, 33.58) * mm, "end": v(68.97, 42.21) * mm, "construction": true});
            skLineSegment(sketch, "E93", {"start": v(68.97, 42.21) * mm, "end": v(68.01, 42.15) * mm, "construction": true});
            skLineSegment(sketch, "E94", {"start": v(68.01, 42.15) * mm, "end": v(59.29, 37.12) * mm, "construction": true});
            skCircle(sketch, "E95", {"center": v(69.72, 45.34) * mm, "radius": 10.88 * mm, "construction": true});
            skLineSegment(sketch, "E96", {"start": v(76.62, 55) * mm, "end": v(74.15, 45.78) * mm});
            skLineSegment(sketch, "E97", {"start": v(80.58, 44.78) * mm, "end": v(72.84, 44.78) * mm, "construction": true});
            skArc(sketch, "E98", {"start": v(81.58, 44.73) * mm, "mid": v(81.31, 45.47) * mm, "end": v(80.59, 45.78) * mm});
            skArc(sketch, "E99", {"start": v(67.98, 34.6) * mm, "mid": v(68.2, 33.84) * mm, "end": v(68.9, 33.48) * mm});
            skLineSegment(sketch, "E100", {"start": v(81.67, 45.78) * mm, "end": v(74.15, 45.78) * mm});
            skLineSegment(sketch, "E101", {"start": v(72.84, 44.78) * mm, "end": v(76.53, 58.54) * mm, "construction": true});
            skArc(sketch, "E102", {"start": v(60.52, 37.83) * mm, "mid": v(61.24, 37.34) * mm, "end": v(62.07, 37.6) * mm});
            skArc(sketch, "E103", {"start": v(76.3, 54) * mm, "mid": v(76.4, 54.92) * mm, "end": v(75.73, 55.54) * mm});
            skArc(sketch, "E104", {"start": v(3.96, 15.99) * mm, "mid": v(2.46, 16.73) * mm, "end": v(2.36, 15.07) * mm});
            skArc(sketch, "E105", {"start": v(4.59, 18.92) * mm, "mid": v(3.2, 18) * mm, "end": v(4.59, 17.08) * mm});
            skArc(sketch, "E106", {"start": v(6.35, 26.6) * mm, "mid": v(6.93, 27.5) * mm, "end": v(6.35, 28.4) * mm});
            skArc(sketch, "E107", {"start": v(3.41, 31.34) * mm, "mid": v(3.62, 29.77) * mm, "end": v(5.09, 30.38) * mm});
            skPoint(sketch, "E108.orphan", {"position": v(5.2, 18) * mm});
            skArc(sketch, "E109.trimOffspring", {"start": v(4.7, 17.13) * mm, "mid": v(5.2, 18) * mm, "end": v(4.7, 18.87) * mm});
            skPoint(sketch, "E110.orphan", {"position": v(3.46, 15) * mm});
            skArc(sketch, "E111.trimOffspring", {"start": v(2.46, 15) * mm, "mid": v(3.46, 15) * mm, "end": v(3.96, 15.87) * mm});
            skPoint(sketch, "E112.orphan", {"position": v(3.46, 21) * mm});
            skArc(sketch, "E113.trimOffspring", {"start": v(2.36, 20.93) * mm, "mid": v(2.46, 19.27) * mm, "end": v(3.96, 20.01) * mm});
            skArc(sketch, "E114.trimOffspring", {"start": v(3.62, 23.5) * mm, "mid": v(4.62, 23.5) * mm, "end": v(5.12, 24.37) * mm});
            skPoint(sketch, "E115.orphan", {"position": v(4.62, 23.5) * mm});
            skArc(sketch, "E116.trimOffspring", {"start": v(6.2, 28.46) * mm, "mid": v(4.93, 27.5) * mm, "end": v(6.2, 26.54) * mm});
            skArc(sketch, "E117.trimOffspring", {"start": v(5.12, 30.63) * mm, "mid": v(4.62, 31.5) * mm, "end": v(3.62, 31.5) * mm});
            skPoint(sketch, "E118.orphan", {"position": v(4.62, 31.5) * mm});
            skPoint(sketch, "E119.orphan", {"position": v(6.93, 27.5) * mm});
            skArc(sketch, "E120.trimOffspring", {"start": v(7.79, 40) * mm, "mid": v(6.66, 39) * mm, "end": v(7.79, 38) * mm});
            skPoint(sketch, "E121.orphan", {"position": v(8.66, 39) * mm});
            skArc(sketch, "E122", {"start": v(6.27, 34.87) * mm, "mid": v(5.77, 34) * mm, "end": v(4.77, 34) * mm});
            skArc(sketch, "E123", {"start": v(8.16, 39.87) * mm, "mid": v(8.66, 39) * mm, "end": v(8.16, 38.13) * mm});
            skPoint(sketch, "E124.orphan", {"position": v(5.77, 44) * mm});
            skLineSegment(sketch, "E125.trimOffspring", {"start": v(4.77, 34) * mm, "end": v(0, 34) * mm});
            skArc(sketch, "E126.trimOffspring", {"start": v(9.38, 53.5) * mm, "mid": v(8.4, 52.5) * mm, "end": v(9.38, 51.5) * mm});
            skArc(sketch, "E127", {"start": v(5.93, 46.5) * mm, "mid": v(6.93, 46.5) * mm, "end": v(7.43, 47.37) * mm});
            skArc(sketch, "E128", {"start": v(5.93, 58.5) * mm, "mid": v(6.93, 58.5) * mm, "end": v(7.43, 57.63) * mm});
            skPoint(sketch, "E129.orphan", {"position": v(6.93, 46.5) * mm});
            skPoint(sketch, "E130.orphan", {"position": v(10.4, 52.5) * mm});
            skPoint(sketch, "E131.orphan", {"position": v(6.93, 58.5) * mm});
            skCircle(sketch, "E132", {"center": v(69.72, 45.34) * mm, "radius": 1 * mm});
            skCircle(sketch, "E133", {"center": v(69.72, 45.34) * mm, "radius": 0.5 * mm});
            skLineSegment(sketch, "E134", {"start": v(68.98, 44.66) * mm, "end": v(60.97, 53.38) * mm});
            skLineSegment(sketch, "E135", {"start": v(68.98, 44.66) * mm, "end": v(70.45, 46.01) * mm, "construction": true});
            skLineSegment(sketch, "E136", {"start": v(70.45, 46.01) * mm, "end": v(62.44, 54.73) * mm});
            skLineSegment(sketch, "E137", {"start": v(62.2, 56.47) * mm, "end": v(64.9, 53.52) * mm, "construction": true});
            skLineSegment(sketch, "E138", {"start": v(64.9, 53.52) * mm, "end": v(61.96, 50.81) * mm, "construction": true});
            skLineSegment(sketch, "E139", {"start": v(61.96, 50.81) * mm, "end": v(59.15, 53.88) * mm, "construction": true});
            skArc(sketch, "E140", {"start": v(64.63, 53.83) * mm, "mid": v(64.94, 54.4) * mm, "end": v(64.82, 55.06) * mm});
            skArc(sketch, "E141.trimOffspring", {"start": v(63.42, 55.41) * mm, "mid": v(62.96, 54.7) * mm, "end": v(63.21, 53.89) * mm});
            skArc(sketch, "E142", {"start": v(61.74, 52.53) * mm, "mid": v(60.95, 52.86) * mm, "end": v(60.2, 52.46) * mm});
            skArc(sketch, "E143.trimOffspring", {"start": v(60.44, 51.03) * mm, "mid": v(61.08, 50.86) * mm, "end": v(61.68, 51.12) * mm});
            skLineSegment(sketch, "E144", {"start": v(0, 63.5) * mm, "end": v(88.9, 0) * mm, "construction": true});
            skLineSegment(sketch, "E145", {"start": v(0, 0) * mm, "end": v(88.9, 63.5) * mm, "construction": true});
            skCircle(sketch, "E146", {"center": v(23.45, 38.75) * mm, "radius": 6.82 * mm});
            skCircle(sketch, "E147", {"center": v(44.45, 31.75) * mm, "radius": 1 * mm});
            skSolve(sketch);
        }
        {
            var Q0;
            Q0=makeQuery(id+"F8.imprint","IMPRINT",FACE,{"disambiguationData":[TD([[makeQuery(id+"F8.imprint","IMPRINT",EDGE,{"derivedFrom":sQuery(id+"F8.wireOp",EDGE,"E72")}),1.0]])]});
            var Q1;
            Q1=makeQuery(id+"F8.imprint","IMPRINT",FACE,{"disambiguationData":[TD([[makeQuery(id+"F8.imprint","IMPRINT",EDGE,{"derivedFrom":sQuery(id+"F8.wireOp",EDGE,"E73")}),1.0]])]});
            var Q2;
            Q2=makeQuery(id+"F8.imprint","IMPRINT",FACE,{"disambiguationData":[TD([[makeQuery(id+"F8.imprint","IMPRINT",EDGE,{"derivedFrom":sQuery(id+"F8.wireOp",EDGE,"E74")}),1.0]])]});
            var Q3;
            Q3=makeQuery(id+"F8.imprint","IMPRINT",FACE,{"disambiguationData":[TD([[makeQuery(id+"F8.imprint","IMPRINT",EDGE,{"derivedFrom":sQuery(id+"F8.wireOp",EDGE,"E75")}),1.0]])]});
            var Q4;
            Q4=makeQuery(id+"F8.imprint","IMPRINT",FACE,{"disambiguationData":[TD([[makeQuery(id+"F8.imprint","IMPRINT",EDGE,{"derivedFrom":sQuery(id+"F8.wireOp",EDGE,"E81")}),1.0]])]});
            var Q5;
            Q5=makeQuery(id+"F8.imprint","IMPRINT",FACE,{"disambiguationData":[TD([[makeQuery(id+"F8.imprint","IMPRINT",EDGE,{"derivedFrom":sQuery(id+"F8.wireOp",EDGE,"E76")}),1.0]])]});
            var Q6;
            Q6=makeQuery(id+"F8.imprint","IMPRINT",FACE,{"disambiguationData":[TD([[makeQuery(id+"F8.imprint","IMPRINT",EDGE,{"derivedFrom":sQuery(id+"F8.wireOp",EDGE,"E77")}),1.0]])]});
            var Q7;
            Q7=makeQuery(id+"F8.imprint","IMPRINT",FACE,{"disambiguationData":[TD([[makeQuery(id+"F8.imprint","IMPRINT",EDGE,{"derivedFrom":sQuery(id+"F8.wireOp",EDGE,"E78")}),1.0]])]});
            var Q8;
            Q8=makeQuery(id+"F8.imprint","IMPRINT",FACE,{"disambiguationData":[TD([[makeQuery(id+"F8.imprint","IMPRINT",EDGE,{"derivedFrom":sQuery(id+"F8.wireOp",EDGE,"E79")}),1.0]])]});
            var Q9;
            Q9=makeQuery(id+"F8.imprint","IMPRINT",FACE,{"disambiguationData":[TD([[makeQuery(id+"F8.imprint","IMPRINT",EDGE,{"derivedFrom":sQuery(id+"F8.wireOp",EDGE,"E80")}),1.0]])]});
            var Q10;
            Q10=makeQuery(id+"F8.imprint","IMPRINT",FACE,{"disambiguationData":[TD([[makeQuery(id+"F8.imprint","IMPRINT",EDGE,{"derivedFrom":sQuery(id+"F8.wireOp",EDGE,"E82")}),1.0]])]});
            var Q11;
            Q11=makeQuery(id+"F8.imprint","IMPRINT",FACE,{"disambiguationData":[TD([[makeQuery(id+"F8.imprint","IMPRINT",EDGE,{"derivedFrom":sQuery(id+"F8.wireOp",EDGE,"E71")}),1.0]])]});
            var Q12;
            Q12=makeQuery(id+"F8.imprint","IMPRINT",FACE,{"disambiguationData":[TD([[makeQuery(id+"F8.imprint","IMPRINT",EDGE,{"derivedFrom":sQuery(id+"F8.wireOp",EDGE,"E70")}),1.0]])]});
            var Q13;
            Q13=makeQuery(id+"F8.imprint","IMPRINT",FACE,{"disambiguationData":[TD([[makeQuery(id+"F8.imprint","IMPRINT",EDGE,{"derivedFrom":sQuery(id+"F8.wireOp",EDGE,"E69")}),1.0]])]});
            var Q14;
            Q14=makeQuery(id+"F8.imprint","IMPRINT",FACE,{"disambiguationData":[TD([[makeQuery(id+"F8.imprint","IMPRINT",EDGE,{"derivedFrom":sQuery(id+"F8.wireOp",EDGE,"E68")}),1.0]])]});
            var Q15;
            Q15=makeQuery(id+"F8.imprint","IMPRINT",FACE,{"disambiguationData":[TD([[makeQuery(id+"F8.imprint","IMPRINT",EDGE,{"derivedFrom":sQuery(id+"F8.wireOp",EDGE,"E67")}),1.0]])]});
            var Q16;
            Q16=makeQuery(id+"F8.imprint","IMPRINT",FACE,{"disambiguationData":[TD([[makeQuery(id+"F8.imprint","IMPRINT",EDGE,{"derivedFrom":sQuery(id+"F8.wireOp",EDGE,"E66")}),1.0]])]});
            var Q17;
            Q17=makeQuery(id+"F8.imprint","IMPRINT",FACE,{"disambiguationData":[TD([[makeQuery(id+"F8.imprint","IMPRINT",EDGE,{"derivedFrom":sQuery(id+"F8.wireOp",EDGE,"E65")}),1.0]])]});
            var Q18;
            Q18=makeQuery(id+"F8.imprint","IMPRINT",FACE,{"disambiguationData":[TD([[makeQuery(id+"F8.imprint","IMPRINT",EDGE,{"derivedFrom":sQuery(id+"F8.wireOp",EDGE,"E64")}),1.0]])]});
            var Q19;
            Q19=makeQuery(id+"F8.imprint","IMPRINT",FACE,{"disambiguationData":[TD([[makeQuery(id+"F8.imprint","IMPRINT",EDGE,{"derivedFrom":sQuery(id+"F8.wireOp",EDGE,"E63")}),1.0]])]});
            var Q20;
            {var subQ0=sQuery(id+"F8.wireOp",EDGE,"E85");var subQ2=sQuery(id+"F8.wireOp",EDGE,"E58.4");var subQ4=makeQuery(id+"F8.imprint","INTERSECT",VERTEX,{"derivedFrom":[subQ2,subQ0]});Q20=makeQuery(id+"F8.imprint","IMPRINT",FACE,{"disambiguationData":[TD([[makeQuery(id+"F8.imprint","IMPRINT",EDGE,{"disambiguationData":[TD([[subQ4,-1.0]])],"derivedFrom":subQ0}),1.0]])]});}
            var Q21;
            {var subQ0=sQuery(id+"F8.wireOp",EDGE,"E86");var subQ2=sQuery(id+"F8.wireOp",EDGE,"E60.4");var subQ4=makeQuery(id+"F8.imprint","INTERSECT",VERTEX,{"derivedFrom":[subQ2,subQ0]});Q21=makeQuery(id+"F8.imprint","IMPRINT",FACE,{"disambiguationData":[TD([[makeQuery(id+"F8.imprint","IMPRINT",EDGE,{"disambiguationData":[TD([[subQ4,-1.0]])],"derivedFrom":subQ0}),1.0]])]});}
            var Q22;
            {var subQ3=sQuery(id+"F8.wireOp",EDGE,"E59.0");Q22=makeQuery(id+"F8.imprint","IMPRINT",FACE,{"disambiguationData":[TD([[makeQuery(id+"F8.imprint","IMPRINT",EDGE,{"derivedFrom":subQ3}),-1.0]])]});}
            var Q23;
            {var subQ1=sQuery(id+"F8.wireOp",EDGE,"E61.0");Q23=makeQuery(id+"F8.imprint","IMPRINT",FACE,{"disambiguationData":[TD([[makeQuery(id+"F8.imprint","IMPRINT",EDGE,{"derivedFrom":subQ1}),-1.0]])]});}
            var Q24;
            {var subQ4=sQuery(id+"F8.wireOp",EDGE,"E98");Q24=makeQuery(id+"F8.imprint","IMPRINT",FACE,{"disambiguationData":[TD([[makeQuery(id+"F8.imprint","IMPRINT",EDGE,{"derivedFrom":subQ4}),1.0]])]});}
            var Q25;
            Q25=makeQuery(id+"F8.imprint","IMPRINT",FACE,{"disambiguationData":[TD([[makeQuery(id+"F8.imprint","IMPRINT",EDGE,{"derivedFrom":sQuery(id+"F8.wireOp",EDGE,"E133")}),1.0]])]});
            var Q26;
            Q26=makeQuery(id+"F8.imprint","IMPRINT",FACE,{"disambiguationData":[TD([[makeQuery(id+"F8.imprint","IMPRINT",EDGE,{"derivedFrom":sQuery(id+"F8.wireOp",EDGE,"E146")}),1.0]])]});
            var Q27;
            Q27=makeQuery(id+"F8.imprint","IMPRINT",FACE,{"disambiguationData":[TD([[makeQuery(id+"F8.imprint","IMPRINT",EDGE,{"derivedFrom":sQuery(id+"F8.wireOp",EDGE,"E147")}),1.0]])]});
            extrude(context, id + "F9", {"entities" : qUnion([Q0, Q1, Q2, Q3, Q4, Q5, Q6, Q7, Q8, Q9, Q10, Q11, Q12, Q13, Q14, Q15, Q16, Q17, Q18, Q19, Q20, Q21, Q22, Q23, Q24, Q25, Q26, Q27]), "operationType" : NewBodyOperationType.REMOVE, "oppositeDirection" : true, "depth" : 25 * mm});
        }
        {
            var Q0;
            Q0=makeQuery(id+"F2.imprint","IMPRINT",FACE,{"disambiguationData":[TD([[makeQuery(id+"F2.imprint","IMPRINT",EDGE,{"derivedFrom":sQuery(id+"F2.wireOp",EDGE,"E14.sketch_text.stroke-0")}),-1.0]])]});
            var sketch = newSketch(context, id + "F10", { "sketchPlane" : qUnion([Q0])});
            skPoint(sketch, "E148.0", {"position": v(0, 63.5) * mm});
            skLineSegment(sketch, "E149", {"start": v(0, 60.5) * mm, "end": v(4, 63.5) * mm});
            skLineSegment(sketch, "E150", {"start": v(4, 63.5) * mm, "end": v(0, 63.5) * mm});
            skLineSegment(sketch, "E151", {"start": v(0, 60.5) * mm, "end": v(0, 63.5) * mm});
            skSolve(sketch);
        }
        {
            var Q0;
            Q0 = qSketchRegion(id + "F10", true);
            extrude(context, id + "F11", {"entities" : qUnion([Q0]), "operationType" : NewBodyOperationType.REMOVE, "oppositeDirection" : true, "depth" : 0.38 * mm});
        }
        {
            var Q0;
            {var subQ13=sQuery(id+"F3.wireOp",EDGE,"E39.sketch_text.stroke-0");Q0=makeQuery(id+"F3.imprint","IMPRINT",FACE,{"disambiguationData":[TD([[makeQuery(id+"F3.imprint","IMPRINT",EDGE,{"derivedFrom":subQ13}),-1.0]])]});}
            var sketch = newSketch(context, id + "F12", { "sketchPlane" : qUnion([Q0])});
            skLineSegment(sketch, "E152.0", {"start": v(0, -60.5) * mm, "end": v(4, -63.5) * mm});
            skLineSegment(sketch, "E153", {"start": v(4, -63.5) * mm, "end": v(0, -63.5) * mm});
            skLineSegment(sketch, "E154", {"start": v(0, -63.5) * mm, "end": v(0, -60.5) * mm});
            skSolve(sketch);
        }
        {
            var Q0;
            Q0=makeQuery(id+"F12.imprint","IMPRINT",FACE,{"disambiguationData":[TD([[makeQuery(id+"F12.imprint","IMPRINT",EDGE,{"derivedFrom":sQuery(id+"F12.wireOp",EDGE,"E152.0")}),-1.0]])]});
            extrude(context, id + "F13", {"entities" : qUnion([Q0]), "operationType" : NewBodyOperationType.REMOVE, "oppositeDirection" : true, "depth" : 0.38 * mm});
        }
        {
            var Q0;
            Q0=makeQuery(id+"F11.boolean.opBoolean","COPY",EDGE,{"derivedFrom":makeQuery(id+"F11.opExtrude","CAP_EDGE",EDGE,{"disambiguationData":[OSD([sQuery(id+"F10.wireOp",EDGE,"E149")])],"isStart":false})});
            var Q1;
            Q1=makeQuery(id+"F13.boolean.opBoolean","COPY",EDGE,{"derivedFrom":makeQuery(id+"F13.opExtrude","CAP_EDGE",EDGE,{"disambiguationData":[OSD([sQuery(id+"F12.wireOp",EDGE,"E152.0")])],"isStart":false})});
            fillet(context, id + "F14", {"entities" : qUnion([Q0, Q1]), "radius" : 1 * mm, "tangentPropagation" : true, "allowEdgeOverflow" : false});
        }
    });
